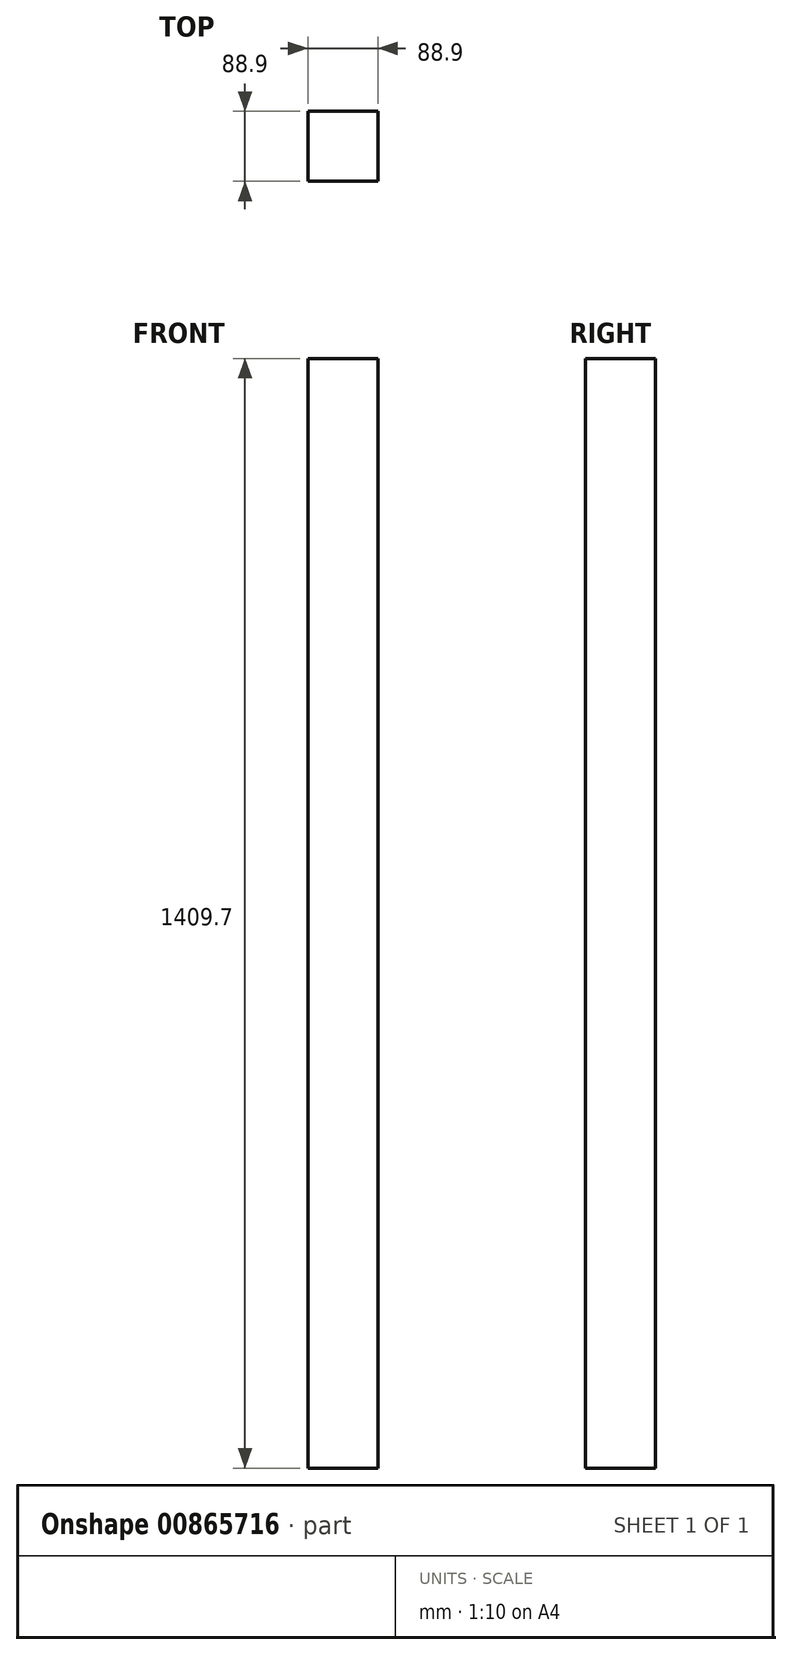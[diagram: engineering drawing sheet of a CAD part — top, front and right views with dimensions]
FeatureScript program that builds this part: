
annotation { "Feature Type Name" : "Feature", "Feature Type Description" : "" }
export const myFeature = defineFeature(function(context is Context, id is Id, definition is map)
    precondition{}
    {
        {
            var Q0;
            Q0=qCreatedBy(makeId("Top.planeOp"),FACE);
            var sketch = newSketch(context, id + "F0", { "sketchPlane" : qUnion([Q0])});
            skLineSegment(sketch, "E0.bottom", {"start": v(0, 0) * mm, "end": v(88.9, 0) * mm});
            skLineSegment(sketch, "E0.top", {"start": v(0, 88.9) * mm, "end": v(88.9, 88.9) * mm});
            skLineSegment(sketch, "E0.left", {"start": v(0, 0) * mm, "end": v(0, 88.9) * mm});
            skLineSegment(sketch, "E0.right", {"start": v(88.9, 0) * mm, "end": v(88.9, 88.9) * mm});
            skSolve(sketch);
        }
        {
            var Q0;
            Q0=makeQuery(id+"F0.imprint","IMPRINT",FACE,{"disambiguationData":[TD([[makeQuery(id+"F0.imprint","IMPRINT",EDGE,{"derivedFrom":sQuery(id+"F0.wireOp",EDGE,"E0.bottom")}),1.0]])]});
            extrude(context, id + "F1", {"entities" : qUnion([Q0]), "depth" : 1409.7 * mm, "offsetDistance" : 25.4 * mm});
        }
    });
